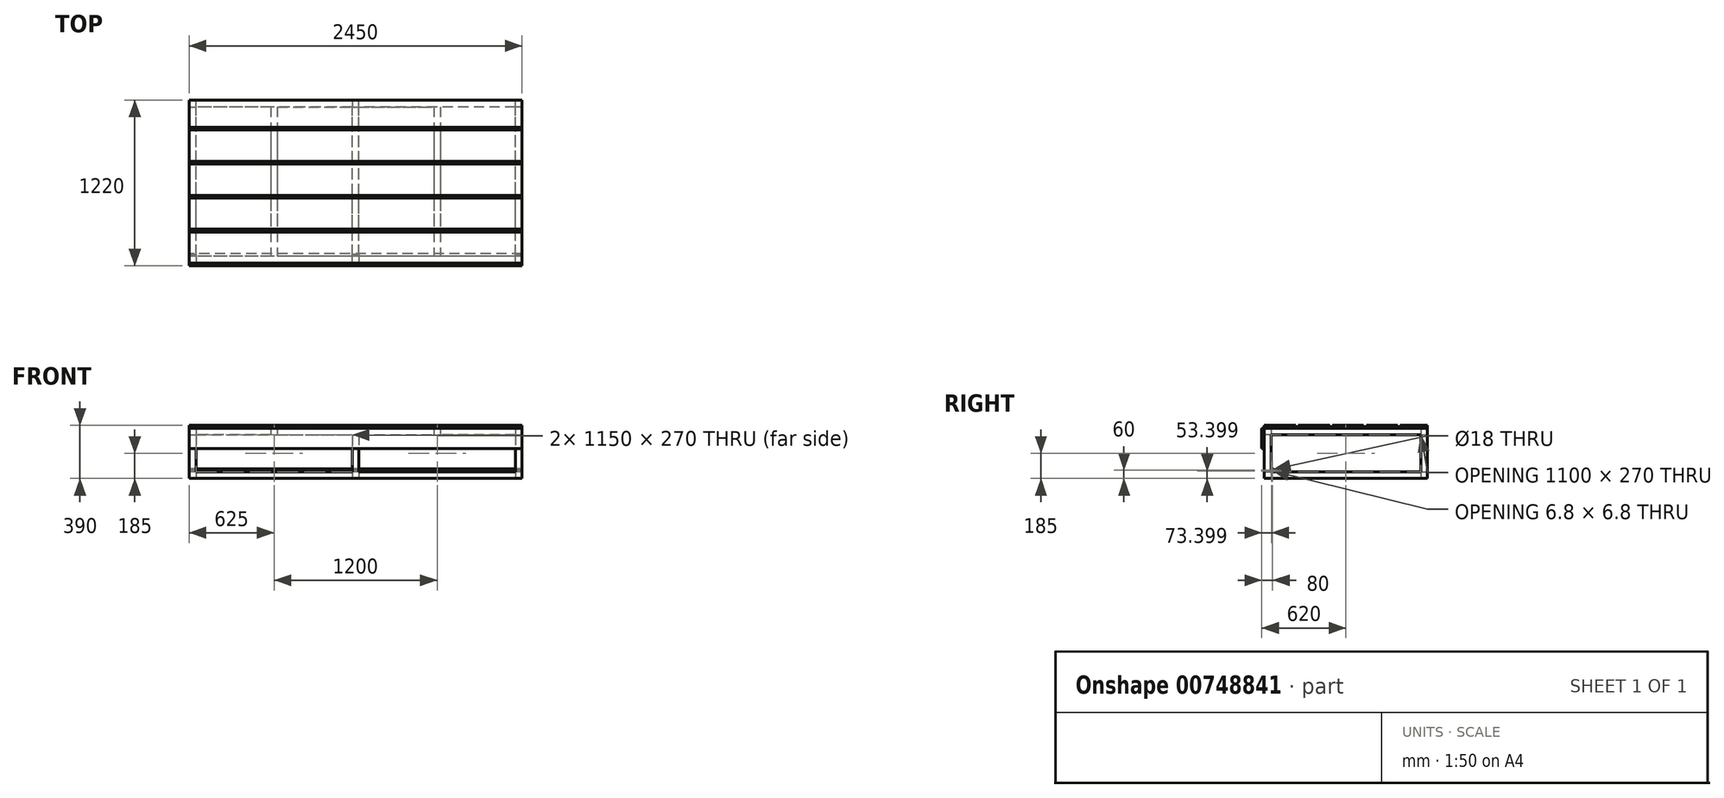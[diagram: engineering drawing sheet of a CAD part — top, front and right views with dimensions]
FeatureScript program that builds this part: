
annotation { "Feature Type Name" : "Feature", "Feature Type Description" : "" }
export const myFeature = defineFeature(function(context is Context, id is Id, definition is map)
    precondition{}
    {
        {
            var Q0;
            Q0=qCreatedBy(makeId("Top.planeOp"),FACE);
            var sketch = newSketch(context, id + "F0", { "sketchPlane" : qUnion([Q0])});
            skLineSegment(sketch, "E0.bottom", {"start": v(1225, -600) * mm, "end": v(-1225, -600) * mm});
            skLineSegment(sketch, "E0.top", {"start": v(1225, 600) * mm, "end": v(-1225, 600) * mm});
            skLineSegment(sketch, "E0.left", {"start": v(1225, -600) * mm, "end": v(1225, 600) * mm});
            skLineSegment(sketch, "E0.right", {"start": v(-1225, -600) * mm, "end": v(-1225, 600) * mm});
            skPoint(sketch, "E0.middle", {"position": v(0, 0) * mm});
            skLineSegment(sketch, "E1.0", {"start": v(1225, 550) * mm, "end": v(-1225, 550) * mm});
            skLineSegment(sketch, "E2.0", {"start": v(1227.5, -600) * mm, "end": v(1227.5, 600) * mm});
            skLineSegment(sketch, "E3.0", {"start": v(1175, -600) * mm, "end": v(1175, 600) * mm});
            skLineSegment(sketch, "E4.0", {"start": v(1225, -550) * mm, "end": v(-1225, -550) * mm});
            skLineSegment(sketch, "E5.0", {"start": v(-1175, -600) * mm, "end": v(-1175, 600) * mm});
            skLineSegment(sketch, "E6", {"start": v(0, 0) * mm, "end": v(0, 550) * mm});
            skLineSegment(sketch, "E7", {"start": v(0, 0) * mm, "end": v(0, -550) * mm});
            skLineSegment(sketch, "E8.0", {"start": v(25, 0) * mm, "end": v(25, 550) * mm});
            skLineSegment(sketch, "E9.0", {"start": v(-25, 0) * mm, "end": v(-25, 550) * mm});
            skLineSegment(sketch, "E10.0", {"start": v(-25, 0) * mm, "end": v(-25, -550) * mm});
            skLineSegment(sketch, "E11.0", {"start": v(25, 0) * mm, "end": v(25, -550) * mm});
            skSolve(sketch);
        }
        {
            var Q0;
            Q0=qSketchRegion(id+"F0",true);
            var Q1;
            {var subQ1=sQuery(id+"F0.wireOp",EDGE,"E6");Q1=makeQuery(id+"F0.imprint","IMPRINT",FACE,{"disambiguationData":[TD([[makeQuery(id+"F0.imprint","IMPRINT",EDGE,{"derivedFrom":subQ1}),-1.0]])]});}
            var Q2;
            {var subQ3=sQuery(id+"F0.wireOp",EDGE,"E6");Q2=makeQuery(id+"F0.imprint","IMPRINT",FACE,{"disambiguationData":[TD([[makeQuery(id+"F0.imprint","IMPRINT",EDGE,{"derivedFrom":subQ3}),1.0]])]});}
            extrude(context, id + "F1", {"entities" : qUnion([Q0, Q1, Q2]), "depth" : 50 * mm, "offsetDistance" : 25 * mm});
        }
        {
            var Q0;
            Q0=makeQuery(id+"F1.opExtrude","CAP_FACE",FACE,{"disambiguationData":[OSD([sQuery(id+"F0.wireOp",EDGE,"E0.bottom"),sQuery(id+"F0.wireOp",EDGE,"E0.top"),sQuery(id+"F0.wireOp",EDGE,"E0.left"),sQuery(id+"F0.wireOp",EDGE,"E0.right"),sQuery(id+"F0.wireOp",EDGE,"E1.0"),sQuery(id+"F0.wireOp",EDGE,"E3.0"),sQuery(id+"F0.wireOp",EDGE,"E4.0"),sQuery(id+"F0.wireOp",EDGE,"E5.0"),sQuery(id+"F0.wireOp",EDGE,"E8.0"),sQuery(id+"F0.wireOp",EDGE,"E9.0"),sQuery(id+"F0.wireOp",EDGE,"E10.0"),sQuery(id+"F0.wireOp",EDGE,"E11.0")])],"isStart":false});
            var sketch = newSketch(context, id + "F2", { "sketchPlane" : qUnion([Q0])});
            skLineSegment(sketch, "E12", {"start": v(-25, 550) * mm, "end": v(25, 550) * mm});
            skLineSegment(sketch, "E13", {"start": v(25, 550) * mm, "end": v(25, 600) * mm});
            skLineSegment(sketch, "E14", {"start": v(25, 600) * mm, "end": v(-25, 600) * mm});
            skLineSegment(sketch, "E15", {"start": v(-25, 600) * mm, "end": v(-25, 550) * mm});
            skLineSegment(sketch, "E16", {"start": v(-1175, 550) * mm, "end": v(-1175, 600) * mm});
            skLineSegment(sketch, "E17", {"start": v(-1175, 600) * mm, "end": v(-1225, 600) * mm});
            skLineSegment(sketch, "E18", {"start": v(-1225, 600) * mm, "end": v(-1225, 550) * mm});
            skLineSegment(sketch, "E19", {"start": v(-1225, 550) * mm, "end": v(-1175, 550) * mm});
            skLineSegment(sketch, "E20", {"start": v(-1175, -550) * mm, "end": v(-1175, -600) * mm});
            skLineSegment(sketch, "E21", {"start": v(-1175, -600) * mm, "end": v(-1225, -600) * mm});
            skLineSegment(sketch, "E22", {"start": v(-1225, -600) * mm, "end": v(-1225, -550) * mm});
            skLineSegment(sketch, "E23", {"start": v(-1225, -550) * mm, "end": v(-1175, -550) * mm});
            skLineSegment(sketch, "E24", {"start": v(-25, -550) * mm, "end": v(25, -550) * mm});
            skLineSegment(sketch, "E25", {"start": v(25, -550) * mm, "end": v(25, -600) * mm});
            skLineSegment(sketch, "E26", {"start": v(25, -600) * mm, "end": v(-25, -600) * mm});
            skPoint(sketch, "E26.endSnap0", {"position": v(0, -600) * mm});
            skLineSegment(sketch, "E27", {"start": v(-25, -600) * mm, "end": v(-25, -550) * mm});
            skLineSegment(sketch, "E28", {"start": v(1175, -550) * mm, "end": v(1225, -550) * mm});
            skLineSegment(sketch, "E29", {"start": v(1225, -550) * mm, "end": v(1225, -600) * mm});
            skLineSegment(sketch, "E30", {"start": v(1225, -600) * mm, "end": v(1175, -600) * mm});
            skLineSegment(sketch, "E31", {"start": v(1175, -600) * mm, "end": v(1175, -550) * mm});
            skLineSegment(sketch, "E32", {"start": v(1175, 550) * mm, "end": v(1175, 600) * mm});
            skLineSegment(sketch, "E33", {"start": v(1175, 600) * mm, "end": v(1225, 600) * mm});
            skLineSegment(sketch, "E34", {"start": v(1225, 600) * mm, "end": v(1225, 550) * mm});
            skLineSegment(sketch, "E35", {"start": v(1225, 550) * mm, "end": v(1175, 550) * mm});
            skSolve(sketch);
        }
        {
            var Q0;
            Q0=qSketchRegion(id+"F2",true);
            extrude(context, id + "F3", {"entities" : qUnion([Q0]), "operationType" : NewBodyOperationType.ADD, "depth" : 270 * mm, "offsetDistance" : 25 * mm});
        }
        {
            var Q0;
            Q0=makeQuery(id+"F3.opExtrude","CAP_FACE",FACE,{"disambiguationData":[OSD([sQuery(id+"F2.wireOp",EDGE,"E12"),sQuery(id+"F2.wireOp",EDGE,"E13"),sQuery(id+"F2.wireOp",EDGE,"E14"),sQuery(id+"F2.wireOp",EDGE,"E15")])],"isStart":false});
            var sketch = newSketch(context, id + "F4", { "sketchPlane" : qUnion([Q0])});
            skLineSegment(sketch, "E36.bottom", {"start": v(-1225, 600) * mm, "end": v(1225, 600) * mm});
            skLineSegment(sketch, "E36.top", {"start": v(-1225, -600) * mm, "end": v(1225, -600) * mm});
            skLineSegment(sketch, "E36.left", {"start": v(-1225, 600) * mm, "end": v(-1225, -600) * mm});
            skLineSegment(sketch, "E36.right", {"start": v(1225, 600) * mm, "end": v(1225, -600) * mm});
            skLineSegment(sketch, "E37.bottom", {"start": v(1175, -550) * mm, "end": v(-1175, -550) * mm});
            skLineSegment(sketch, "E37.top", {"start": v(1175, 550) * mm, "end": v(-1175, 550) * mm});
            skLineSegment(sketch, "E37.left", {"start": v(1175, -550) * mm, "end": v(1175, 550) * mm});
            skLineSegment(sketch, "E37.right", {"start": v(-1175, -550) * mm, "end": v(-1175, 550) * mm});
            skLineSegment(sketch, "E38.bottom", {"start": v(-25, 550) * mm, "end": v(25, 550) * mm});
            skLineSegment(sketch, "E38.top", {"start": v(-25, -550) * mm, "end": v(25, -550) * mm});
            skLineSegment(sketch, "E38.left", {"start": v(-25, 550) * mm, "end": v(-25, -550) * mm});
            skLineSegment(sketch, "E38.right", {"start": v(25, 550) * mm, "end": v(25, -550) * mm});
            skLineSegment(sketch, "E39", {"start": v(-25, 550) * mm, "end": v(-1175, 550) * mm});
            skLineSegment(sketch, "E40", {"start": v(-600, 550) * mm, "end": v(-600, -550) * mm});
            skLineSegment(sketch, "E41.0", {"start": v(-625, 550) * mm, "end": v(-625, -550) * mm});
            skLineSegment(sketch, "E42.0", {"start": v(-575, 550) * mm, "end": v(-575, -550) * mm});
            skLineSegment(sketch, "E43", {"start": v(25, 550) * mm, "end": v(1175, 550) * mm});
            skLineSegment(sketch, "E44", {"start": v(600, 550) * mm, "end": v(600, -550) * mm});
            skLineSegment(sketch, "E45.0", {"start": v(575, 550) * mm, "end": v(575, -550) * mm});
            skLineSegment(sketch, "E46.0", {"start": v(625, 550) * mm, "end": v(625, -550) * mm});
            skSolve(sketch);
        }
        {
            var Q0;
            Q0=qSketchRegion(id+"F4",true);
            var Q1;
            {var subQ0=sQuery(id+"F4.wireOp",EDGE,"E40");Q1=makeQuery(id+"F4.imprint","IMPRINT",FACE,{"disambiguationData":[TD([[makeQuery(id+"F4.imprint","IMPRINT",EDGE,{"derivedFrom":subQ0}),1.0]])]});}
            var Q2;
            {var subQ0=sQuery(id+"F4.wireOp",EDGE,"E40");Q2=makeQuery(id+"F4.imprint","IMPRINT",FACE,{"disambiguationData":[TD([[makeQuery(id+"F4.imprint","IMPRINT",EDGE,{"derivedFrom":subQ0}),-1.0]])]});}
            var Q3;
            {var subQ0=sQuery(id+"F4.wireOp",EDGE,"E44");Q3=makeQuery(id+"F4.imprint","IMPRINT",FACE,{"disambiguationData":[TD([[makeQuery(id+"F4.imprint","IMPRINT",EDGE,{"derivedFrom":subQ0}),1.0]])]});}
            var Q4;
            {var subQ0=sQuery(id+"F4.wireOp",EDGE,"E44");Q4=makeQuery(id+"F4.imprint","IMPRINT",FACE,{"disambiguationData":[TD([[makeQuery(id+"F4.imprint","IMPRINT",EDGE,{"derivedFrom":subQ0}),-1.0]])]});}
            var Q5;
            Q5=makeQuery(id+"F4.imprint","IMPRINT",FACE,{"disambiguationData":[TD([[makeQuery(id+"F4.imprint","IMPRINT",EDGE,{"derivedFrom":sQuery(id+"F4.wireOp",EDGE,"E38.bottom")}),-1.0]])]});
            extrude(context, id + "F5", {"entities" : qUnion([Q0, Q1, Q2, Q3, Q4, Q5]), "operationType" : NewBodyOperationType.ADD, "depth" : 50 * mm, "offsetDistance" : 25 * mm});
        }
        {
            var Q0;
            Q0=makeQuery(id+"F5.boolean.opBoolean","MERGE",FACE,{"derivedFrom":[makeQuery(id+"F3.boolean.opBoolean","MERGE",FACE,{"derivedFrom":[makeQuery(id+"F1.opExtrude","SWEPT_FACE",FACE,{"disambiguationData":[OSD([sQuery(id+"F0.wireOp",EDGE,"E0.right")])]}),makeQuery(id+"F3.opExtrude","SWEPT_FACE",FACE,{"disambiguationData":[OSD([sQuery(id+"F2.wireOp",EDGE,"E18")])]}),makeQuery(id+"F3.opExtrude","SWEPT_FACE",FACE,{"disambiguationData":[OSD([sQuery(id+"F2.wireOp",EDGE,"E22")])]})]}),makeQuery(id+"F5.opExtrude","SWEPT_FACE",FACE,{"disambiguationData":[OSD([sQuery(id+"F4.wireOp",EDGE,"E36.left")])]})]});
            var sketch = newSketch(context, id + "F6", { "sketchPlane" : qUnion([Q0])});
            skLineSegment(sketch, "E47", {"start": v(550, 50) * mm, "end": v(550, 60) * mm});
            skLineSegment(sketch, "E48", {"start": v(550, 60) * mm, "end": v(540, 60) * mm});
            skCircle(sketch, "E49", {"center": v(540, 60) * mm, "radius": 10.5 * mm});
            skCircle(sketch, "E50", {"center": v(540, 60) * mm, "radius": 9 * mm});
            skSolve(sketch);
        }
        {
            var Q0;
            Q0=qSketchRegion(id+"F6",true);
            extrude(context, id + "F7", {"entities" : qUnion([Q0]), "operationType" : NewBodyOperationType.ADD, "oppositeDirection" : true, "depth" : 2450 * mm, "offsetDistance" : 25 * mm});
        }
        {
            var Q0;
            Q0=makeQuery(id+"F5.boolean.opBoolean","MERGE",FACE,{"derivedFrom":[makeQuery(id+"F3.boolean.opBoolean","MERGE",FACE,{"derivedFrom":[makeQuery(id+"F1.opExtrude","SWEPT_FACE",FACE,{"disambiguationData":[OSD([sQuery(id+"F0.wireOp",EDGE,"E0.bottom")])]}),makeQuery(id+"F3.opExtrude","SWEPT_FACE",FACE,{"disambiguationData":[OSD([sQuery(id+"F2.wireOp",EDGE,"E21")])]}),makeQuery(id+"F3.opExtrude","SWEPT_FACE",FACE,{"disambiguationData":[OSD([sQuery(id+"F2.wireOp",EDGE,"E26")])]}),makeQuery(id+"F3.opExtrude","SWEPT_FACE",FACE,{"disambiguationData":[OSD([sQuery(id+"F2.wireOp",EDGE,"E30")])]})]}),makeQuery(id+"F5.opExtrude","SWEPT_FACE",FACE,{"disambiguationData":[OSD([sQuery(id+"F4.wireOp",EDGE,"E36.top")])]})]});
            var sketch = newSketch(context, id + "F8", { "sketchPlane" : qUnion([Q0])});
            skLineSegment(sketch, "E51.bottom", {"start": v(1225, 370) * mm, "end": v(-1275, 370) * mm});
            skLineSegment(sketch, "E51.top", {"start": v(1225, 220) * mm, "end": v(-1275, 220) * mm});
            skLineSegment(sketch, "E51.left", {"start": v(1225, 370) * mm, "end": v(1225, 220) * mm});
            skLineSegment(sketch, "E51.right", {"start": v(-1275, 370) * mm, "end": v(-1275, 220) * mm});
            skLineSegment(sketch, "E52", {"start": v(-1225, 370) * mm, "end": v(-1275, 370) * mm});
            skSolve(sketch);
        }
        {
            var Q0;
            Q0=qSketchRegion(id+"F8",true);
            extrude(context, id + "F9", {"entities" : qUnion([Q0]), "depth" : 20 * mm, "offsetDistance" : 25 * mm});
        }
        {
            var Q0;
            Q0=makeQuery(id+"F5.opExtrude","CAP_FACE",FACE,{"disambiguationData":[OSD([sQuery(id+"F4.wireOp",EDGE,"E36.bottom"),sQuery(id+"F4.wireOp",EDGE,"E36.top"),sQuery(id+"F4.wireOp",EDGE,"E36.left"),sQuery(id+"F4.wireOp",EDGE,"E36.right"),sQuery(id+"F4.wireOp",EDGE,"E37.bottom"),sQuery(id+"F4.wireOp",EDGE,"E37.left"),sQuery(id+"F4.wireOp",EDGE,"E37.right"),sQuery(id+"F4.wireOp",EDGE,"E38.left"),sQuery(id+"F4.wireOp",EDGE,"E38.right"),sQuery(id+"F4.wireOp",EDGE,"E39"),sQuery(id+"F4.wireOp",EDGE,"E41.0"),sQuery(id+"F4.wireOp",EDGE,"E42.0"),sQuery(id+"F4.wireOp",EDGE,"E43"),sQuery(id+"F4.wireOp",EDGE,"E45.0"),sQuery(id+"F4.wireOp",EDGE,"E46.0")])],"isStart":false});
            var sketch = newSketch(context, id + "F10", { "sketchPlane" : qUnion([Q0])});
            skLineSegment(sketch, "E53.bottom", {"start": v(1225, 600) * mm, "end": v(-1275, 600) * mm});
            skLineSegment(sketch, "E53.top", {"start": v(1225, -600) * mm, "end": v(-1275, -600) * mm});
            skLineSegment(sketch, "E53.left", {"start": v(1225, 600) * mm, "end": v(1225, -600) * mm});
            skLineSegment(sketch, "E53.right", {"start": v(-1275, 600) * mm, "end": v(-1275, -600) * mm});
            skSolve(sketch);
        }
        {
            var Q0;
            Q0=qSketchRegion(id+"F10",true);
            extrude(context, id + "F11", {"entities" : qUnion([Q0]), "depth" : 20 * mm, "offsetDistance" : 25 * mm});
        }
        {
            var Q0;
            Q0=makeQuery(id+"F11.opExtrude","SWEPT_FACE",FACE,{"disambiguationData":[OSD([sQuery(id+"F10.wireOp",EDGE,"E53.right")])]});
            var sketch = newSketch(context, id + "F12", { "sketchPlane" : qUnion([Q0])});
            skLineSegment(sketch, "E54", {"start": v(620, 370) * mm, "end": v(600, 370) * mm});
            skLineSegment(sketch, "E55", {"start": v(600, 370) * mm, "end": v(600, 390) * mm});
            skLineSegment(sketch, "E56", {"start": v(600, 390) * mm, "end": v(620, 390) * mm});
            skLineSegment(sketch, "E57", {"start": v(620, 390) * mm, "end": v(620, 370) * mm});
            skLineSegment(sketch, "E58.1.0.0", {"start": v(370, 390) * mm, "end": v(370, 370) * mm});
            skLineSegment(sketch, "E58.1.0.1", {"start": v(350, 390) * mm, "end": v(370, 390) * mm});
            skLineSegment(sketch, "E58.1.0.2", {"start": v(350, 370) * mm, "end": v(350, 390) * mm});
            skLineSegment(sketch, "E58.1.0.3", {"start": v(370, 370) * mm, "end": v(350, 370) * mm});
            skLineSegment(sketch, "E58.2.0.0", {"start": v(120, 390) * mm, "end": v(120, 370) * mm});
            skLineSegment(sketch, "E58.2.0.1", {"start": v(100, 390) * mm, "end": v(120, 390) * mm});
            skLineSegment(sketch, "E58.2.0.2", {"start": v(100, 370) * mm, "end": v(100, 390) * mm});
            skLineSegment(sketch, "E58.2.0.3", {"start": v(120, 370) * mm, "end": v(100, 370) * mm});
            skLineSegment(sketch, "E58.3.0.0", {"start": v(-130, 390) * mm, "end": v(-130, 370) * mm});
            skLineSegment(sketch, "E58.3.0.1", {"start": v(-150, 390) * mm, "end": v(-130, 390) * mm});
            skLineSegment(sketch, "E58.3.0.2", {"start": v(-150, 370) * mm, "end": v(-150, 390) * mm});
            skLineSegment(sketch, "E58.3.0.3", {"start": v(-130, 370) * mm, "end": v(-150, 370) * mm});
            skLineSegment(sketch, "E58.4.0.0", {"start": v(-380, 390) * mm, "end": v(-380, 370) * mm});
            skLineSegment(sketch, "E58.4.0.1", {"start": v(-400, 390) * mm, "end": v(-380, 390) * mm});
            skLineSegment(sketch, "E58.4.0.2", {"start": v(-400, 370) * mm, "end": v(-400, 390) * mm});
            skLineSegment(sketch, "E58.4.0.3", {"start": v(-380, 370) * mm, "end": v(-400, 370) * mm});
            skLineSegment(sketch, "E58.direction1", {"start": v(620, 370) * mm, "end": v(370, 370) * mm, "construction": true});
            skSolve(sketch);
        }
        {
            var Q0;
            Q0=makeQuery(id+"F12.imprint","IMPRINT",FACE,{"disambiguationData":[TD([[makeQuery(id+"F12.imprint","IMPRINT",EDGE,{"derivedFrom":sQuery(id+"F12.wireOp",EDGE,"E54")}),-1.0]])]});
            var Q1;
            Q1=makeQuery(id+"F12.imprint","IMPRINT",FACE,{"disambiguationData":[TD([[makeQuery(id+"F12.imprint","IMPRINT",EDGE,{"derivedFrom":sQuery(id+"F12.wireOp",EDGE,"E58.1.0.0")}),-1.0]])]});
            var Q2;
            Q2=makeQuery(id+"F12.imprint","IMPRINT",FACE,{"disambiguationData":[TD([[makeQuery(id+"F12.imprint","IMPRINT",EDGE,{"derivedFrom":sQuery(id+"F12.wireOp",EDGE,"E58.2.0.0")}),-1.0]])]});
            var Q3;
            Q3=makeQuery(id+"F12.imprint","IMPRINT",FACE,{"disambiguationData":[TD([[makeQuery(id+"F12.imprint","IMPRINT",EDGE,{"derivedFrom":sQuery(id+"F12.wireOp",EDGE,"E58.3.0.0")}),-1.0]])]});
            var Q4;
            Q4=makeQuery(id+"F12.imprint","IMPRINT",FACE,{"disambiguationData":[TD([[makeQuery(id+"F12.imprint","IMPRINT",EDGE,{"derivedFrom":sQuery(id+"F12.wireOp",EDGE,"E58.4.0.0")}),-1.0]])]});
            var Q5;
            Q5=makeQuery(id+"F11.opExtrude","SWEPT_FACE",FACE,{"disambiguationData":[OSD([sQuery(id+"F10.wireOp",EDGE,"E53.left")])]});
            extrude(context, id + "F13", {"entities" : qUnion([Q0, Q1, Q2, Q3, Q4]), "operationType" : NewBodyOperationType.REMOVE, "endBound" : BoundingType.UP_TO_SURFACE, "oppositeDirection" : true, "depth" : 25 * mm, "endBoundEntityFace" : qUnion([Q5]), "offsetDistance" : 25 * mm});
        }
        {
            var Q0;
            Q0=makeQuery(id+"F9.opExtrude","CAP_FACE",FACE,{"disambiguationData":[OSD([sQuery(id+"F8.wireOp",EDGE,"E51.bottom"),sQuery(id+"F8.wireOp",EDGE,"E51.top"),sQuery(id+"F8.wireOp",EDGE,"E51.left"),sQuery(id+"F8.wireOp",EDGE,"E51.right"),sQuery(id+"F8.wireOp",EDGE,"E52")])],"isStart":false});
            var sketch = newSketch(context, id + "F14", { "sketchPlane" : qUnion([Q0])});
            skLineSegment(sketch, "E59.bottom", {"start": v(-1225, 220) * mm, "end": v(-1275, 220) * mm});
            skLineSegment(sketch, "E59.top", {"start": v(-1225, 390) * mm, "end": v(-1275, 390) * mm});
            skLineSegment(sketch, "E59.left", {"start": v(-1225, 220) * mm, "end": v(-1225, 390) * mm});
            skLineSegment(sketch, "E59.right", {"start": v(-1275, 220) * mm, "end": v(-1275, 390) * mm});
            skSolve(sketch);
        }
        {
            var Q0;
            Q0 = qSketchRegion(id + "F14", true);
            var Q1;
            Q1=makeQuery(id+"F11.opExtrude","SWEPT_FACE",FACE,{"disambiguationData":[OSD([sQuery(id+"F10.wireOp",EDGE,"E53.bottom")])]});
            extrude(context, id + "F15", {"entities" : qUnion([Q0]), "operationType" : NewBodyOperationType.REMOVE, "endBound" : BoundingType.UP_TO_SURFACE, "oppositeDirection" : true, "depth" : 25 * mm, "endBoundEntityFace" : qUnion([Q1]), "offsetDistance" : 25 * mm});
        }
    });
